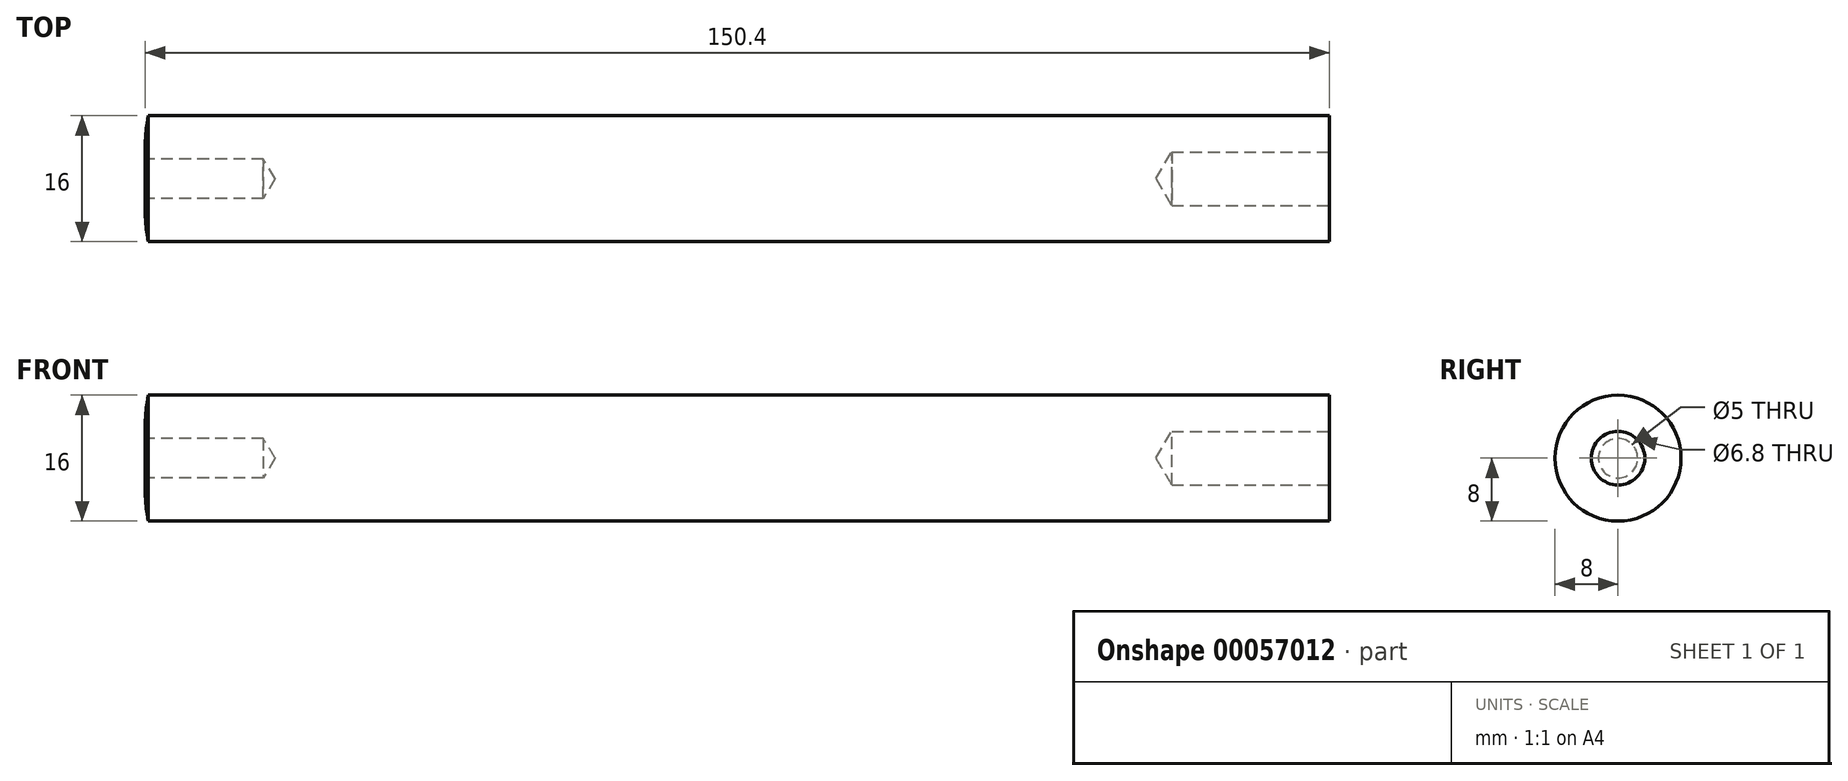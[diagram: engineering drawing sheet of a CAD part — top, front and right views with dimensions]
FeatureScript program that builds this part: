
annotation { "Feature Type Name" : "Feature", "Feature Type Description" : "" }
export const myFeature = defineFeature(function(context is Context, id is Id, definition is map)
    precondition{}
    {
        {
            var Q0;
            Q0=qCreatedBy(makeId("Front.planeOp"),FACE);
            var sketch = newSketch(context, id + "F0", { "sketchPlane" : qUnion([Q0])});
            skLineSegment(sketch, "E0", {"start": v(75.2, 0) * mm, "end": v(-75.2, 0) * mm});
            skLineSegment(sketch, "E1", {"start": v(75.2, 0) * mm, "end": v(75.2, 8) * mm});
            skLineSegment(sketch, "E2", {"start": v(75.2, 8) * mm, "end": v(-74.8, 8) * mm});
            skLineSegment(sketch, "E3", {"start": v(-75.2, 0) * mm, "end": v(-75.2, 4) * mm});
            skArc(sketch, "E4", {"start": v(-74.8, 8) * mm, "mid": v(-75.1, 6.01) * mm, "end": v(-75.2, 4) * mm});
            skPoint(sketch, "E5.orphan", {"position": v(-75.2, 8) * mm});
            skLineSegment(sketch, "E6", {"start": v(-142.12, 0) * mm, "end": v(101.29, 0) * mm, "construction": true});
            skSolve(sketch);
        }
        {
            var Q0;
            Q0 = qSketchRegion(id + "F0", true);
            var Q1;
            Q1=sQuery(id+"F0.wireOp",EDGE,"E6");
            revolve(context, id + "F1", {"entities" : qUnion([Q0]), "axis" : qUnion([Q1]), "revolveType" : RevolveType.FULL});
        }
        {
            var Q0;
            Q0=makeQuery(id+"F1.opRevolve","SWEPT_FACE",FACE,{"disambiguationData":[OSD([sQuery(id+"F0.wireOp",EDGE,"E3")])]});
            var sketch = newSketch(context, id + "F2", { "sketchPlane" : qUnion([Q0])});
            skPoint(sketch, "E7", {"position": v(0, 0) * mm});
            skSolve(sketch);
        }
        {
            var Q0;
            Q0=sQuery(id+"F2.wireOp",VERTEX,"E7");
            var Q1;
            Q1=makeQuery(id+"F1.opRevolve","SWEPT_BODY",BODY,{"disambiguationData":[OSD([sQuery(id+"F0.wireOp",EDGE,"E0"),sQuery(id+"F0.wireOp",EDGE,"E1"),sQuery(id+"F0.wireOp",EDGE,"E2"),sQuery(id+"F0.wireOp",EDGE,"E3"),sQuery(id+"F0.wireOp",EDGE,"E4")])]});
            hole(context, id + "F3", {"style" : HoleStyle.SIMPLE, "holeDiameter" : 5 * mm, "endStyle" : HoleEndStyle.BLIND, "holeDepth" : 15 * mm, "locations" : qUnion([Q0]), "scope" : qUnion([Q1])});
        }
        {
            var Q0;
            Q0=makeQuery(id+"F1.opRevolve","SWEPT_FACE",FACE,{"disambiguationData":[OSD([sQuery(id+"F0.wireOp",EDGE,"E1")])]});
            var sketch = newSketch(context, id + "F4", { "sketchPlane" : qUnion([Q0])});
            skPoint(sketch, "E8", {"position": v(0, 0) * mm});
            skSolve(sketch);
        }
        {
            var Q0;
            Q0=sQuery(id+"F4.wireOp",VERTEX,"E8");
            var Q1;
            Q1=makeQuery(id+"F1.opRevolve","SWEPT_BODY",BODY,{"disambiguationData":[OSD([sQuery(id+"F0.wireOp",EDGE,"E0"),sQuery(id+"F0.wireOp",EDGE,"E1"),sQuery(id+"F0.wireOp",EDGE,"E2"),sQuery(id+"F0.wireOp",EDGE,"E3"),sQuery(id+"F0.wireOp",EDGE,"E4")])]});
            hole(context, id + "F5", {"style" : HoleStyle.SIMPLE, "holeDiameter" : 6.8 * mm, "endStyle" : HoleEndStyle.BLIND, "holeDepth" : 20 * mm, "locations" : qUnion([Q0]), "scope" : qUnion([Q1])});
        }
    });
